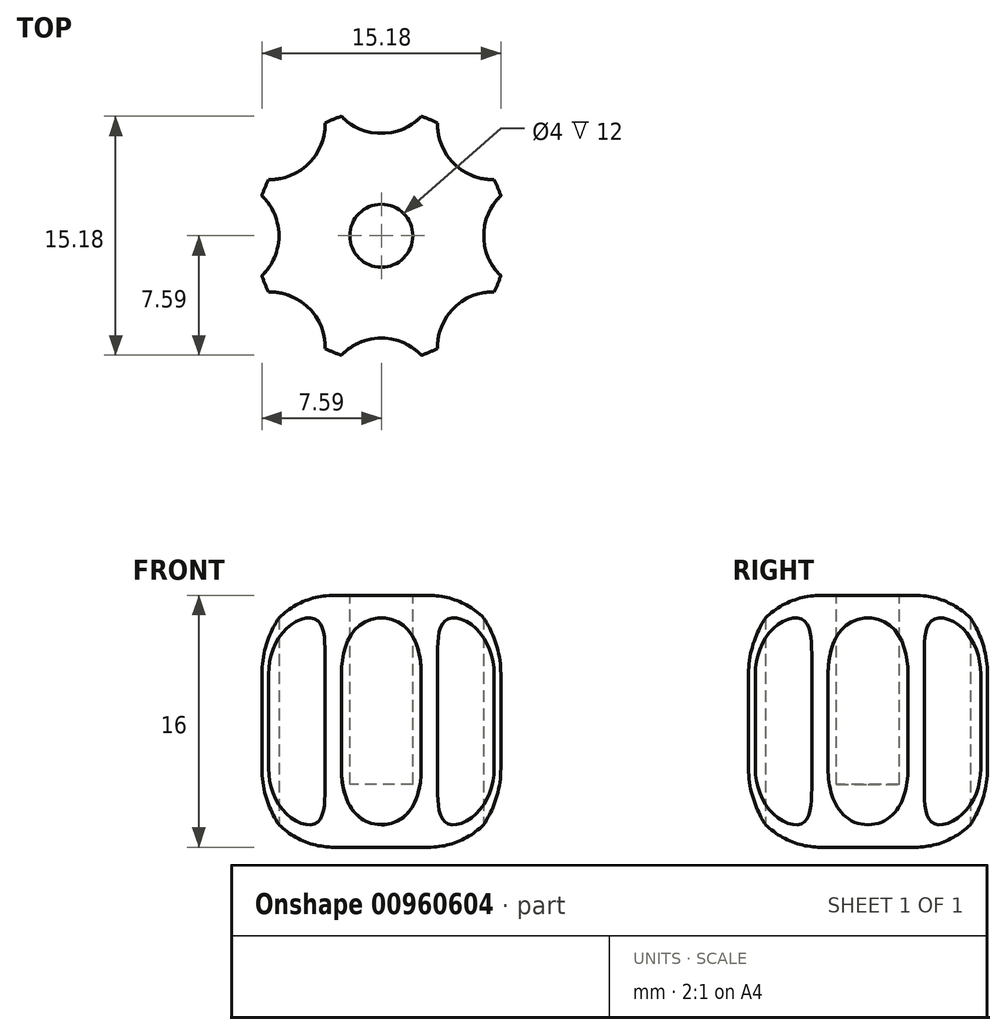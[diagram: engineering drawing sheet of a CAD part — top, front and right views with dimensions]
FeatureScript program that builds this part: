
annotation { "Feature Type Name" : "Feature", "Feature Type Description" : "" }
export const myFeature = defineFeature(function(context is Context, id is Id, definition is map)
    precondition{}
    {
        {
            var Q0;
            Q0=qCreatedBy(makeId("Front.planeOp"),FACE);
            var sketch = newSketch(context, id + "F0", { "sketchPlane" : qUnion([Q0])});
            skLineSegment(sketch, "E0", {"start": v(-2, 16) * mm, "end": v(-2, 4) * mm});
            skLineSegment(sketch, "E1", {"start": v(-2, 4) * mm, "end": v(0, 4) * mm});
            skLineSegment(sketch, "E2", {"start": v(0, 4) * mm, "end": v(0, 0) * mm});
            skLineSegment(sketch, "E3", {"start": v(0, 0) * mm, "end": v(-8, 0) * mm});
            skLineSegment(sketch, "E4", {"start": v(-8, 0) * mm, "end": v(-8, 6) * mm});
            skLineSegment(sketch, "E5", {"start": v(-8, 6) * mm, "end": v(-8, 6) * mm});
            skLineSegment(sketch, "E6", {"start": v(-8, 6) * mm, "end": v(-8, 16) * mm});
            skLineSegment(sketch, "E7", {"start": v(-8, 16) * mm, "end": v(-2, 16) * mm});
            skSolve(sketch);
        }
        {
            var Q0;
            Q0=makeQuery(id+"F0.imprint","IMPRINT",FACE,{"disambiguationData":[TD([[makeQuery(id+"F0.imprint","IMPRINT",EDGE,{"derivedFrom":sQuery(id+"F0.wireOp",EDGE,"E0")}),-1.0]])]});
            var Q1;
            Q1=sQuery(id+"F0.wireOp",EDGE,"E2");
            revolve(context, id + "F1", {"surfaceOperationType" : NewSurfaceOperationType.NEW, "entities" : qUnion([Q0]), "axis" : qUnion([Q1]), "revolveType" : RevolveType.FULL});
        }
        {
            var Q0;
            Q0=makeQuery(id+"F1.opRevolve","SWEPT_EDGE",EDGE,{"disambiguationData":[OSD([sQuery(id+"F0.wireOp",EDGE,"E4"),sQuery(id+"F0.wireOp",EDGE,"E5")])]});
            var Q1;
            Q1=makeQuery(id+"F1.opRevolve","SWEPT_EDGE",EDGE,{"disambiguationData":[OSD([sQuery(id+"F0.wireOp",EDGE,"E3"),sQuery(id+"F0.wireOp",EDGE,"E4")])]});
            var Q2;
            Q2=makeQuery(id+"F1.opRevolve","SWEPT_EDGE",EDGE,{"disambiguationData":[OSD([sQuery(id+"F0.wireOp",EDGE,"E6"),sQuery(id+"F0.wireOp",EDGE,"E7")])]});
            fillet(context, id + "F2", {"entities" : qUnion([Q0, Q1, Q2]), "radius" : 5 * mm, "tangentPropagation" : true, "allowEdgeOverflow" : false});
        }
        {
            var Q0;
            Q0=makeQuery(id+"F1.opRevolve","SWEPT_FACE",FACE,{"disambiguationData":[OSD([sQuery(id+"F0.wireOp",EDGE,"E3")])]});
            var sketch = newSketch(context, id + "F3", { "sketchPlane" : qUnion([Q0])});
            skCircle(sketch, "E8", {"center": v(0, 10) * mm, "radius": 3.5 * mm});
            skCircle(sketch, "E9.1.0", {"center": v(-7.07, 7.07) * mm, "radius": 3.5 * mm});
            skCircle(sketch, "E9.2.0", {"center": v(-10, 0) * mm, "radius": 3.5 * mm});
            skCircle(sketch, "E9.3.0", {"center": v(-7.07, -7.07) * mm, "radius": 3.5 * mm});
            skCircle(sketch, "E9.4.0", {"center": v(0, -10) * mm, "radius": 3.5 * mm});
            skCircle(sketch, "E9.5.0", {"center": v(7.07, -7.07) * mm, "radius": 3.5 * mm});
            skCircle(sketch, "E9.6.0", {"center": v(10, 0) * mm, "radius": 3.5 * mm});
            skCircle(sketch, "E9.7.0", {"center": v(7.07, 7.07) * mm, "radius": 3.5 * mm});
            skPoint(sketch, "E9.center", {"position": v(0, 0) * mm});
            skSolve(sketch);
        }
        {
            var Q0;
            Q0=makeQuery(id+"F3.imprint","IMPRINT",FACE,{"disambiguationData":[TD([[makeQuery(id+"F3.imprint","IMPRINT",EDGE,{"derivedFrom":sQuery(id+"F3.wireOp",EDGE,"E8")}),1.0]])]});
            var Q1;
            Q1=makeQuery(id+"F3.imprint","IMPRINT",FACE,{"disambiguationData":[TD([[makeQuery(id+"F3.imprint","IMPRINT",EDGE,{"derivedFrom":sQuery(id+"F3.wireOp",EDGE,"E9.9.0")}),1.0]])]});
            var Q2;
            Q2=makeQuery(id+"F3.imprint","IMPRINT",FACE,{"disambiguationData":[TD([[makeQuery(id+"F3.imprint","IMPRINT",EDGE,{"derivedFrom":sQuery(id+"F3.wireOp",EDGE,"E9.8.0")}),1.0]])]});
            var Q3;
            Q3=makeQuery(id+"F3.imprint","IMPRINT",FACE,{"disambiguationData":[TD([[makeQuery(id+"F3.imprint","IMPRINT",EDGE,{"derivedFrom":sQuery(id+"F3.wireOp",EDGE,"E9.7.0")}),1.0]])]});
            var Q4;
            Q4=makeQuery(id+"F3.imprint","IMPRINT",FACE,{"disambiguationData":[TD([[makeQuery(id+"F3.imprint","IMPRINT",EDGE,{"derivedFrom":sQuery(id+"F3.wireOp",EDGE,"E9.6.0")}),1.0]])]});
            var Q5;
            Q5=makeQuery(id+"F3.imprint","IMPRINT",FACE,{"disambiguationData":[TD([[makeQuery(id+"F3.imprint","IMPRINT",EDGE,{"derivedFrom":sQuery(id+"F3.wireOp",EDGE,"E9.5.0")}),1.0]])]});
            var Q6;
            Q6=makeQuery(id+"F3.imprint","IMPRINT",FACE,{"disambiguationData":[TD([[makeQuery(id+"F3.imprint","IMPRINT",EDGE,{"derivedFrom":sQuery(id+"F3.wireOp",EDGE,"E9.4.0")}),1.0]])]});
            var Q7;
            Q7=makeQuery(id+"F3.imprint","IMPRINT",FACE,{"disambiguationData":[TD([[makeQuery(id+"F3.imprint","IMPRINT",EDGE,{"derivedFrom":sQuery(id+"F3.wireOp",EDGE,"E9.3.0")}),1.0]])]});
            var Q8;
            Q8=makeQuery(id+"F3.imprint","IMPRINT",FACE,{"disambiguationData":[TD([[makeQuery(id+"F3.imprint","IMPRINT",EDGE,{"derivedFrom":sQuery(id+"F3.wireOp",EDGE,"E9.2.0")}),1.0]])]});
            var Q9;
            Q9=makeQuery(id+"F3.imprint","IMPRINT",FACE,{"disambiguationData":[TD([[makeQuery(id+"F3.imprint","IMPRINT",EDGE,{"derivedFrom":sQuery(id+"F3.wireOp",EDGE,"E9.1.0")}),1.0]])]});
            extrude(context, id + "F4", {"entities" : qUnion([Q0, Q1, Q2, Q3, Q4, Q5, Q6, Q7, Q8, Q9]), "operationType" : NewBodyOperationType.REMOVE, "oppositeDirection" : true, "depth" : 25 * mm, "offsetDistance" : 25 * mm});
        }
    });
